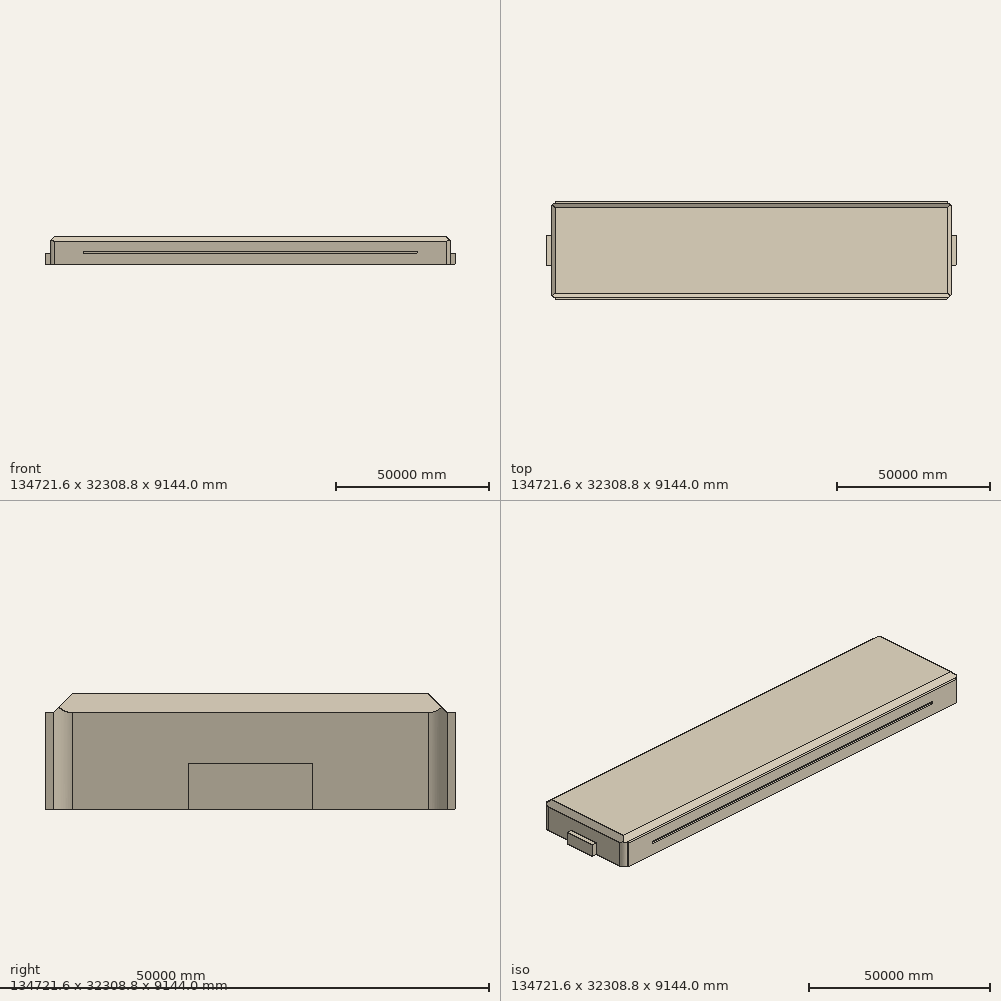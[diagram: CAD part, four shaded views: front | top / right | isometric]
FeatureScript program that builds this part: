
annotation { "Feature Type Name" : "Feature", "Feature Type Description" : "" }
export const myFeature = defineFeature(function(context is Context, id is Id, definition is map)
    precondition{}
    {
        {
            var Q0;
            Q0=qCreatedBy(makeId("Top.planeOp"),FACE);
            var sketch = newSketch(context, id + "F0", { "sketchPlane" : qUnion([Q0])});
            skLineSegment(sketch, "E0.bottom", {"start": v(65836.8, -15544.8) * mm, "end": v(-65836.8, -15544.8) * mm});
            skLineSegment(sketch, "E0.top", {"start": v(65836.8, 15544.8) * mm, "end": v(-65836.8, 15544.8) * mm});
            skLineSegment(sketch, "E0.left", {"start": v(65836.8, -15544.8) * mm, "end": v(65836.8, 15544.8) * mm});
            skLineSegment(sketch, "E0.right", {"start": v(-65836.8, -15544.8) * mm, "end": v(-65836.8, 15544.8) * mm});
            skPoint(sketch, "E0.middle", {"position": v(0, 0) * mm});
            skSolve(sketch);
        }
        {
            var Q0;
            Q0 = qSketchRegion(id + "F0", true);
            extrude(context, id + "F1", {"entities" : qUnion([Q0]), "depth" : 9144 * mm, "offsetDistance" : 25.4 * mm});
        }
        {
            var Q0;
            Q0=makeQuery(id+"F1.opExtrude","CAP_EDGE",EDGE,{"disambiguationData":[OSD([sQuery(id+"F0.wireOp",EDGE,"E0.top")])],"isStart":false});
            var Q1;
            Q1=makeQuery(id+"F1.opExtrude","CAP_EDGE",EDGE,{"disambiguationData":[OSD([sQuery(id+"F0.wireOp",EDGE,"E0.left")])],"isStart":false});
            var Q2;
            Q2=makeQuery(id+"F1.opExtrude","CAP_EDGE",EDGE,{"disambiguationData":[OSD([sQuery(id+"F0.wireOp",EDGE,"E0.bottom")])],"isStart":false});
            var Q3;
            Q3=makeQuery(id+"F1.opExtrude","CAP_EDGE",EDGE,{"disambiguationData":[OSD([sQuery(id+"F0.wireOp",EDGE,"E0.right")])],"isStart":false});
            chamfer(context, id + "F2", {"entities" : qUnion([Q0, Q1, Q2, Q3]), "width" : 1524 * mm, "tangentPropagation" : true});
        }
        {
            var Q0;
            Q0=makeQuery(id+"F1.opExtrude","SWEPT_EDGE",EDGE,{"disambiguationData":[OSD([sQuery(id+"F0.wireOp",EDGE,"E0.bottom"),sQuery(id+"F0.wireOp",EDGE,"E0.right")])]});
            var Q1;
            Q1=makeQuery(id+"F1.opExtrude","SWEPT_EDGE",EDGE,{"disambiguationData":[OSD([sQuery(id+"F0.wireOp",EDGE,"E0.top"),sQuery(id+"F0.wireOp",EDGE,"E0.left")])]});
            var Q2;
            Q2=makeQuery(id+"F1.opExtrude","SWEPT_EDGE",EDGE,{"disambiguationData":[OSD([sQuery(id+"F0.wireOp",EDGE,"E0.bottom"),sQuery(id+"F0.wireOp",EDGE,"E0.left")])]});
            var Q3;
            Q3=makeQuery(id+"F1.opExtrude","SWEPT_EDGE",EDGE,{"disambiguationData":[OSD([sQuery(id+"F0.wireOp",EDGE,"E0.top"),sQuery(id+"F0.wireOp",EDGE,"E0.right")])]});
            fillet(context, id + "F3", {"entities" : qUnion([Q0, Q1, Q2, Q3]), "radius" : 1524 * mm, "tangentPropagation" : true, "allowEdgeOverflow" : false});
        }
        {
            var Q0;
            Q0=makeQuery(id+"F1.opExtrude","SWEPT_FACE",FACE,{"disambiguationData":[OSD([sQuery(id+"F0.wireOp",EDGE,"E0.left")])]});
            var sketch = newSketch(context, id + "F4", { "sketchPlane" : qUnion([Q0])});
            skLineSegment(sketch, "E1.bottom", {"start": v(0, 3657.6) * mm, "end": v(4876.8, 3657.6) * mm});
            skLineSegment(sketch, "E1.top", {"start": v(0, 0) * mm, "end": v(4876.8, 0) * mm});
            skLineSegment(sketch, "E1.left", {"start": v(0, 3657.6) * mm, "end": v(0, 0) * mm});
            skLineSegment(sketch, "E1.right", {"start": v(4876.8, 3657.6) * mm, "end": v(4876.8, 0) * mm});
            skLineSegment(sketch, "E2.bottom", {"start": v(0, 0) * mm, "end": v(-4876.8, 0) * mm});
            skLineSegment(sketch, "E2.top", {"start": v(0, 3657.6) * mm, "end": v(-4876.8, 3657.6) * mm});
            skLineSegment(sketch, "E2.left", {"start": v(0, 0) * mm, "end": v(0, 3657.6) * mm});
            skLineSegment(sketch, "E2.right", {"start": v(-4876.8, 0) * mm, "end": v(-4876.8, 3657.6) * mm});
            skSolve(sketch);
        }
        {
            var Q0;
            Q0 = qSketchRegion(id + "F4", true);
            extrude(context, id + "F5", {"entities" : qUnion([Q0]), "operationType" : NewBodyOperationType.ADD, "depth" : 1524 * mm, "offsetDistance" : 25.4 * mm});
        }
        {
            var Q0;
            Q0=makeQuery(id+"F1.opExtrude","SWEPT_FACE",FACE,{"disambiguationData":[OSD([sQuery(id+"F0.wireOp",EDGE,"E0.right")])]});
            var sketch = newSketch(context, id + "F6", { "sketchPlane" : qUnion([Q0])});
            skLineSegment(sketch, "E3.bottom", {"start": v(0, 3657.6) * mm, "end": v(4876.8, 3657.6) * mm});
            skLineSegment(sketch, "E3.top", {"start": v(0, 0) * mm, "end": v(4876.8, 0) * mm});
            skLineSegment(sketch, "E3.left", {"start": v(0, 3657.6) * mm, "end": v(0, 0) * mm});
            skLineSegment(sketch, "E3.right", {"start": v(4876.8, 3657.6) * mm, "end": v(4876.8, 0) * mm});
            skLineSegment(sketch, "E4.bottom", {"start": v(0, 0) * mm, "end": v(-4876.8, 0) * mm});
            skLineSegment(sketch, "E4.top", {"start": v(0, 3657.6) * mm, "end": v(-4876.8, 3657.6) * mm});
            skLineSegment(sketch, "E4.left", {"start": v(0, 0) * mm, "end": v(0, 3657.6) * mm});
            skLineSegment(sketch, "E4.right", {"start": v(-4876.8, 0) * mm, "end": v(-4876.8, 3657.6) * mm});
            skSolve(sketch);
        }
        {
            var Q0;
            Q0 = qSketchRegion(id + "F6", true);
            extrude(context, id + "F7", {"entities" : qUnion([Q0]), "operationType" : NewBodyOperationType.ADD, "depth" : 1524 * mm, "offsetDistance" : 25.4 * mm});
        }
        {
            var Q0;
            Q0=makeQuery(id+"F1.opExtrude","SWEPT_FACE",FACE,{"disambiguationData":[OSD([sQuery(id+"F0.wireOp",EDGE,"E0.bottom")])]});
            var sketch = newSketch(context, id + "F8", { "sketchPlane" : qUnion([Q0])});
            skLineSegment(sketch, "E5.bottom", {"start": v(55020.6, 4300.52) * mm, "end": v(-55020.6, 4300.52) * mm});
            skLineSegment(sketch, "E5.top", {"start": v(55020.6, 3492.63) * mm, "end": v(-55020.6, 3492.63) * mm});
            skLineSegment(sketch, "E5.left", {"start": v(55020.6, 4300.52) * mm, "end": v(55020.6, 3492.63) * mm});
            skLineSegment(sketch, "E5.right", {"start": v(-55020.6, 4300.52) * mm, "end": v(-55020.6, 3492.63) * mm});
            skPoint(sketch, "E5.middle", {"position": v(0, 3896.58) * mm});
            skSolve(sketch);
        }
        {
            var Q0;
            Q0=makeQuery(id+"F8.imprint","IMPRINT",FACE,{"disambiguationData":[TD([[makeQuery(id+"F8.imprint","IMPRINT",EDGE,{"derivedFrom":sQuery(id+"F8.wireOp",EDGE,"E5.bottom")}),-1.0]])]});
            extrude(context, id + "F9", {"entities" : qUnion([Q0]), "operationType" : NewBodyOperationType.ADD, "depth" : 609.6 * mm, "offsetDistance" : 25.4 * mm});
        }
        {
            var Q0;
            Q0=makeQuery(id+"F1.opExtrude","SWEPT_FACE",FACE,{"disambiguationData":[OSD([sQuery(id+"F0.wireOp",EDGE,"E0.top")])]});
            var sketch = newSketch(context, id + "F10", { "sketchPlane" : qUnion([Q0])});
            skLineSegment(sketch, "E6.bottom", {"start": v(-55020.6, 3123.95) * mm, "end": v(55020.6, 3123.95) * mm});
            skLineSegment(sketch, "E6.top", {"start": v(-55020.6, 3931.84) * mm, "end": v(55020.6, 3931.84) * mm});
            skLineSegment(sketch, "E6.left", {"start": v(-55020.6, 3123.95) * mm, "end": v(-55020.6, 3931.84) * mm});
            skLineSegment(sketch, "E6.right", {"start": v(55020.6, 3123.95) * mm, "end": v(55020.6, 3931.84) * mm});
            skPoint(sketch, "E6.middle", {"position": v(0, 3527.9) * mm});
            skSolve(sketch);
        }
        {
            var Q0;
            Q0=makeQuery(id+"F10.imprint","IMPRINT",FACE,{"disambiguationData":[TD([[makeQuery(id+"F10.imprint","IMPRINT",EDGE,{"derivedFrom":sQuery(id+"F10.wireOp",EDGE,"E6.bottom")}),-1.0]])]});
            extrude(context, id + "F11", {"entities" : qUnion([Q0]), "operationType" : NewBodyOperationType.ADD, "depth" : 609.6 * mm, "offsetDistance" : 25.4 * mm});
        }
    });
